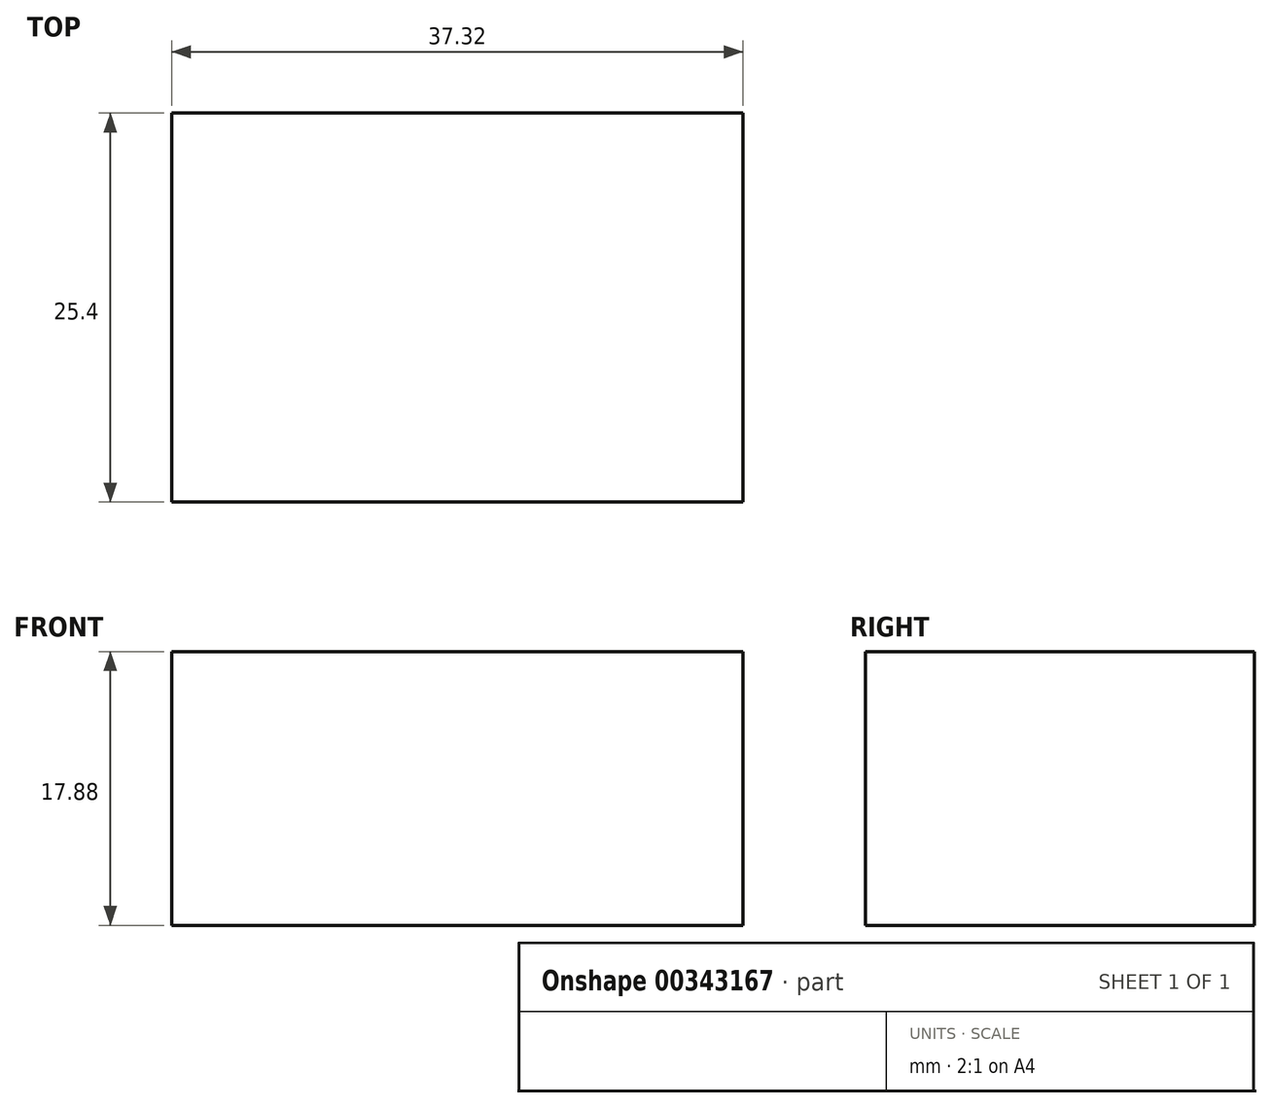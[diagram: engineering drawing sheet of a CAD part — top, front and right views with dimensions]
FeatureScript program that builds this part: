
annotation { "Feature Type Name" : "Feature", "Feature Type Description" : "" }
export const myFeature = defineFeature(function(context is Context, id is Id, definition is map)
    precondition{}
    {
        {
            var Q0;
            Q0=qCreatedBy(makeId("Front.planeOp"),FACE);
            var sketch = newSketch(context, id + "F0", { "sketchPlane" : qUnion([Q0])});
            skLineSegment(sketch, "E0.bottom", {"start": v(0, 0) * mm, "end": v(37.32, 0) * mm});
            skLineSegment(sketch, "E0.top", {"start": v(0, 17.88) * mm, "end": v(37.32, 17.88) * mm});
            skLineSegment(sketch, "E0.left", {"start": v(0, 0) * mm, "end": v(0, 17.88) * mm});
            skLineSegment(sketch, "E0.right", {"start": v(37.32, 0) * mm, "end": v(37.32, 17.88) * mm});
            skSolve(sketch);
        }
        {
            var Q0;
            Q0 = qSketchRegion(id + "F0", true);
            extrude(context, id + "F1", {"entities" : qUnion([Q0]), "depth" : 25.4 * mm});
        }
    });
